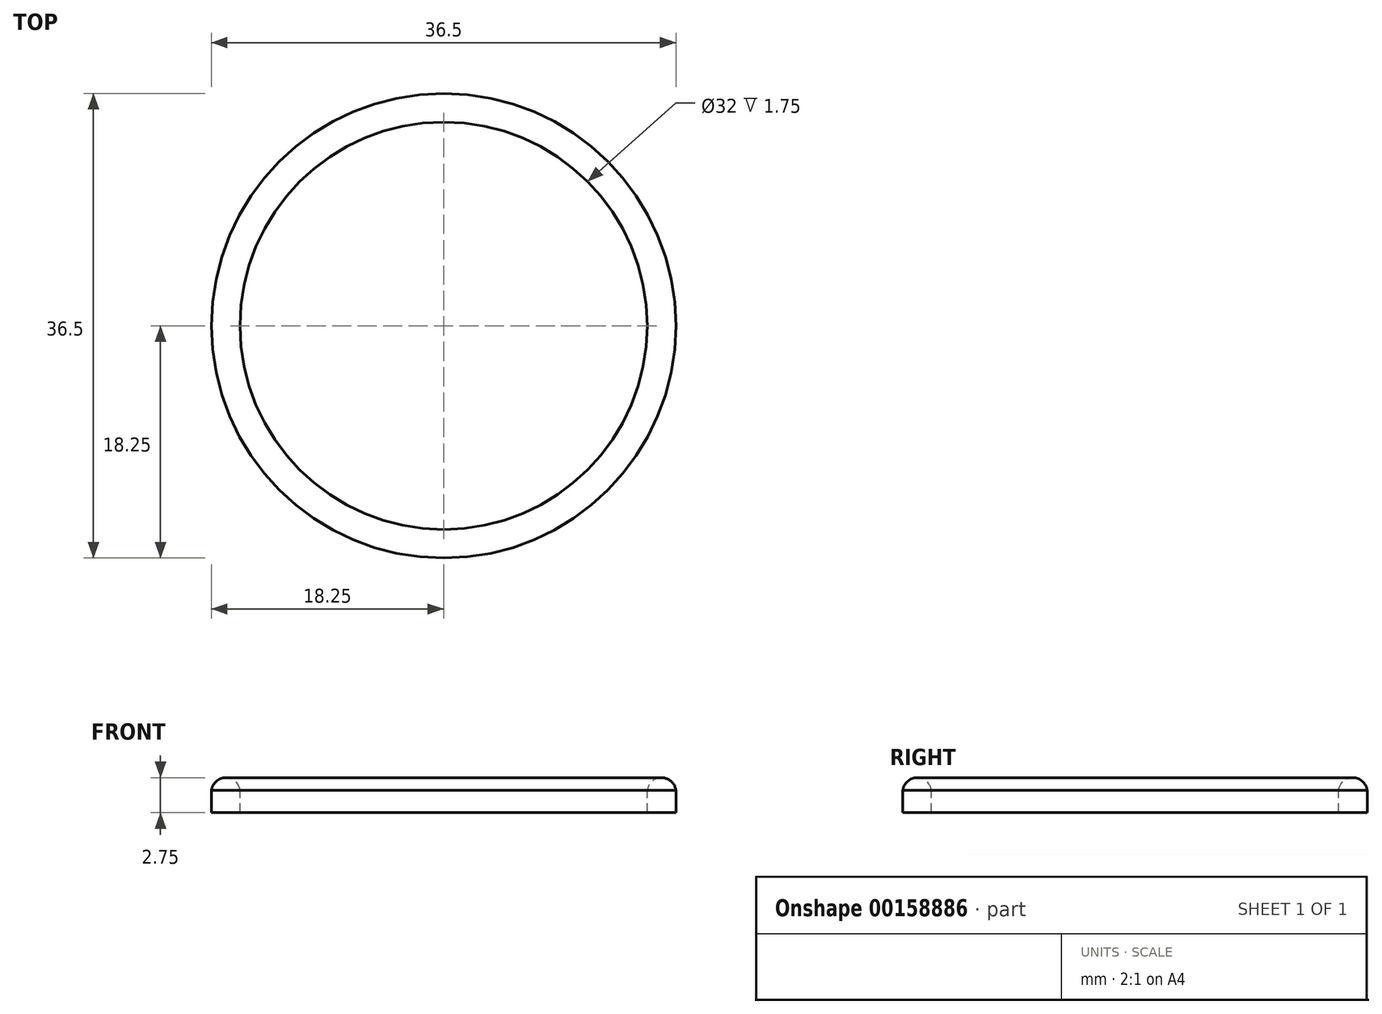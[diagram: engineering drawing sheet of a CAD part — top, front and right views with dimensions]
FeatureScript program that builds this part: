
annotation { "Feature Type Name" : "Feature", "Feature Type Description" : "" }
export const myFeature = defineFeature(function(context is Context, id is Id, definition is map)
    precondition{}
    {
        {
            var Q0;
            Q0=qCreatedBy(makeId("Front.planeOp"),FACE);
            var sketch = newSketch(context, id + "F0", { "sketchPlane" : qUnion([Q0])});
            skLineSegment(sketch, "E0", {"start": v(0, 23.54) * mm, "end": v(0, -27.58) * mm, "construction": true});
            skLineSegment(sketch, "E1.bottom", {"start": v(-18.25, 0) * mm, "end": v(-16, 0) * mm});
            skLineSegment(sketch, "E1.top", {"start": v(-18.25, 1.75) * mm, "end": v(-16, 1.75) * mm});
            skLineSegment(sketch, "E1.left", {"start": v(-18.25, 0) * mm, "end": v(-18.25, 1.75) * mm});
            skLineSegment(sketch, "E1.right", {"start": v(-16, 0) * mm, "end": v(-16, 1.75) * mm});
            skArc(sketch, "E2", {"start": v(-16, 1.75) * mm, "mid": v(-17.12, 2.75) * mm, "end": v(-18.25, 1.75) * mm});
            skPoint(sketch, "E3", {"position": v(-17.12, 1.75) * mm});
            skSolve(sketch);
        }
        {
            var Q0;
            Q0=makeQuery(id+"F0.imprint","IMPRINT",FACE,{"disambiguationData":[TD([[makeQuery(id+"F0.imprint","IMPRINT",EDGE,{"derivedFrom":sQuery(id+"F0.wireOp",EDGE,"E1.bottom")}),1.0]])]});
            var Q1;
            Q1=makeQuery(id+"F0.imprint","IMPRINT",FACE,{"disambiguationData":[TD([[makeQuery(id+"F0.imprint","IMPRINT",EDGE,{"derivedFrom":sQuery(id+"F0.wireOp",EDGE,"E1.top")}),1.0]])]});
            var Q2;
            Q2=sQuery(id+"F0.wireOp",EDGE,"E0");
            revolve(context, id + "F1", {"entities" : qUnion([Q0, Q1]), "axis" : qUnion([Q2]), "revolveType" : RevolveType.FULL});
        }
    });
